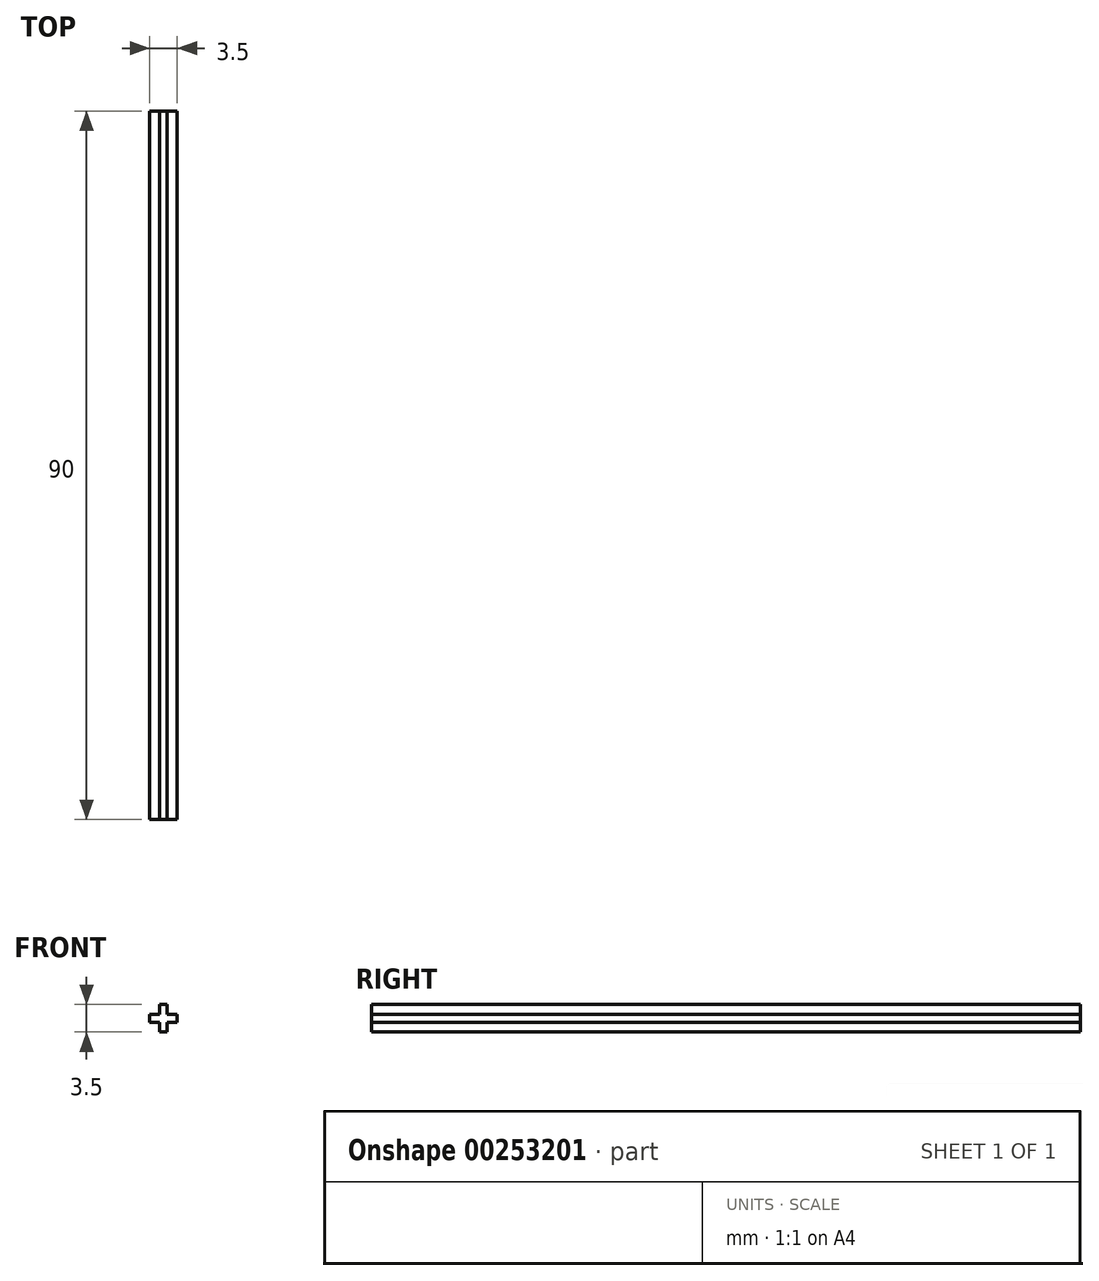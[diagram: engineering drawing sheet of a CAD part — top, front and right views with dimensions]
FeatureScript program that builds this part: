
annotation { "Feature Type Name" : "Feature", "Feature Type Description" : "" }
export const myFeature = defineFeature(function(context is Context, id is Id, definition is map)
    precondition{}
    {
        {
            var Q0;
            Q0=qCreatedBy(makeId("Front.planeOp"),FACE);
            var sketch = newSketch(context, id + "F0", { "sketchPlane" : qUnion([Q0])});
            skLineSegment(sketch, "E0.0", {"start": v(-0.5, 0.5) * mm, "end": v(-0.5, 1.75) * mm});
            skLineSegment(sketch, "E0.1", {"start": v(-0.5, 1.75) * mm, "end": v(0.5, 1.75) * mm});
            skLineSegment(sketch, "E0.2", {"start": v(0.5, 1.75) * mm, "end": v(0.5, 0.5) * mm});
            skLineSegment(sketch, "E0.3", {"start": v(0.5, 0.5) * mm, "end": v(1.75, 0.5) * mm});
            skLineSegment(sketch, "E0.4", {"start": v(1.75, 0.5) * mm, "end": v(1.75, -0.5) * mm});
            skLineSegment(sketch, "E0.5", {"start": v(1.75, -0.5) * mm, "end": v(0.5, -0.5) * mm});
            skLineSegment(sketch, "E0.6", {"start": v(0.5, -0.5) * mm, "end": v(0.5, -1.75) * mm});
            skLineSegment(sketch, "E0.7", {"start": v(0.5, -1.75) * mm, "end": v(-0.5, -1.75) * mm});
            skLineSegment(sketch, "E0.8", {"start": v(-0.5, -1.75) * mm, "end": v(-0.5, -0.5) * mm});
            skLineSegment(sketch, "E0.9", {"start": v(-0.5, -0.5) * mm, "end": v(-1.75, -0.5) * mm});
            skLineSegment(sketch, "E0.10", {"start": v(-1.75, -0.5) * mm, "end": v(-1.75, 0.5) * mm});
            skLineSegment(sketch, "E0.11", {"start": v(-1.75, 0.5) * mm, "end": v(-0.5, 0.5) * mm});
            skLineSegment(sketch, "E1", {"start": v(-0.5, 0.5) * mm, "end": v(0.5, -0.5) * mm, "construction": true});
            skLineSegment(sketch, "E2", {"start": v(-0.5, -0.5) * mm, "end": v(0.5, 0.5) * mm, "construction": true});
            skSolve(sketch);
        }
        {
            var Q0;
            Q0 = qSketchRegion(id + "F0", true);
            extrude(context, id + "F1", {"entities" : qUnion([Q0]), "depth" : 90 * mm});
        }
    });
